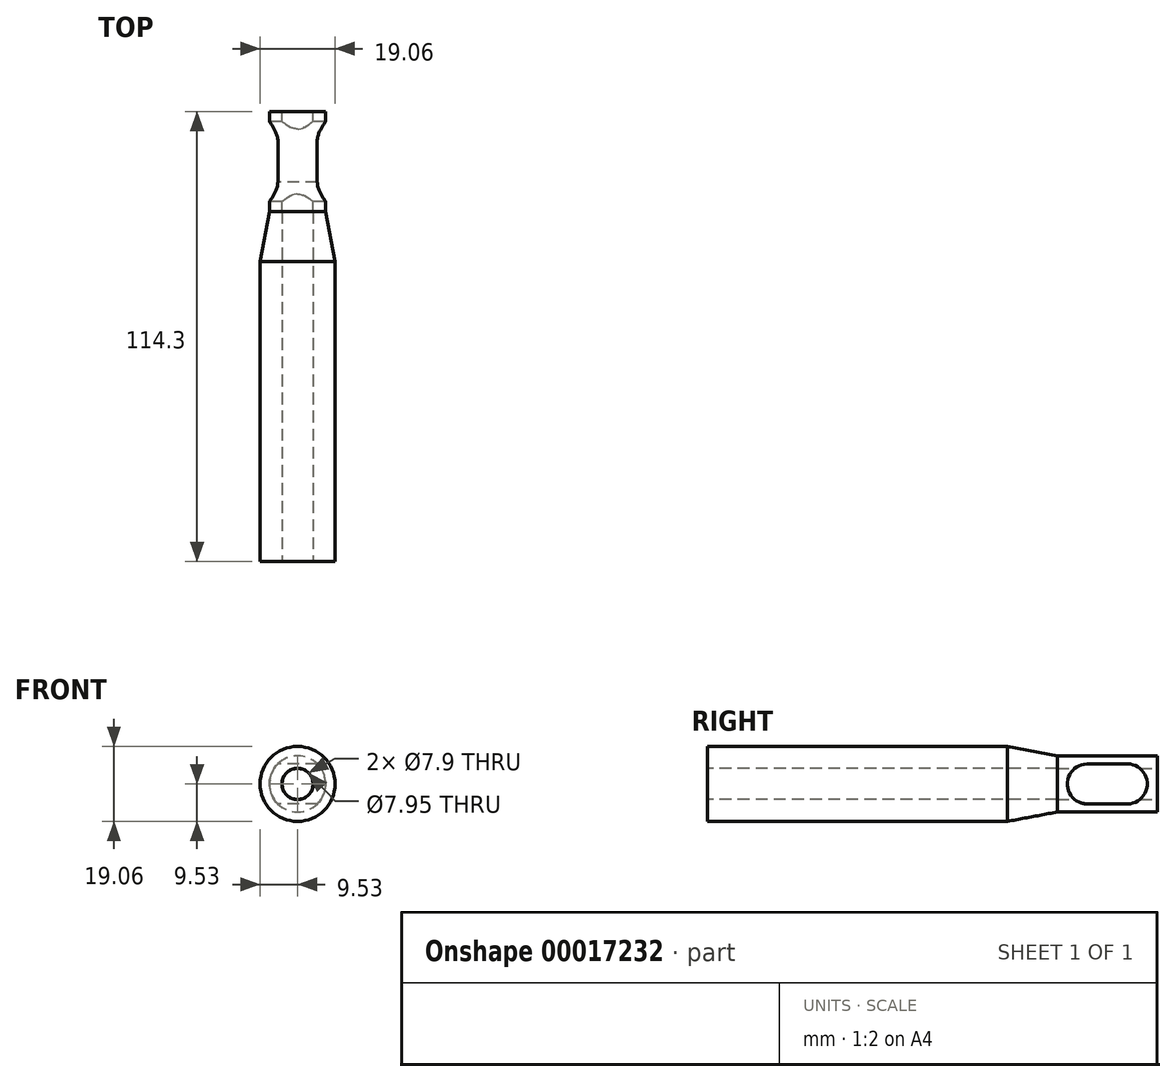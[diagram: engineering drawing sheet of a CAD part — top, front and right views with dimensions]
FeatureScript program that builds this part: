
annotation { "Feature Type Name" : "Feature", "Feature Type Description" : "" }
export const myFeature = defineFeature(function(context is Context, id is Id, definition is map)
    precondition{}
    {
        {
            var Q0;
            Q0=qCreatedBy(makeId("Front.planeOp"),FACE);
            var sketch = newSketch(context, id + "F0", { "sketchPlane" : qUnion([Q0])});
            skCircle(sketch, "E0.0", {"center": v(0, 0) * mm, "radius": 7.12 * mm});
            skSolve(sketch);
        }
        {
            var Q0;
            Q0=qCreatedBy(makeId("Top.planeOp"),FACE);
            var sketch = newSketch(context, id + "F1", { "sketchPlane" : qUnion([Q0])});
            skLineSegment(sketch, "E1", {"start": v(0, 0) * mm, "end": v(0, -25.4) * mm});
            skSolve(sketch);
        }
        {
            var Q0;
            Q0=makeQuery(id+"F0.imprint","IMPRINT",FACE,{"disambiguationData":[TD([[makeQuery(id+"F0.imprint","IMPRINT",EDGE,{"derivedFrom":sQuery(id+"F0.wireOp",EDGE,"093aef5c-26ce-4296-9acc-bf2fb9c0db15")}),-1.0]])]});
            var Q1;
            Q1=makeQuery(id+"F0.imprint","IMPRINT",FACE,{"disambiguationData":[TD([[makeQuery(id+"F0.imprint","IMPRINT",EDGE,{"derivedFrom":sQuery(id+"F0.wireOp",EDGE,"E0.0")}),1.0]])]});
            var Q2;
            Q2=sQuery(id+"F1.wireOp",EDGE,"E1");
            sweep(context, id + "F2", {"profiles" : qUnion([Q0, Q1]), "path" : qUnion([Q2])});
        }
        {
            var Q0;
            Q0=makeQuery(id+"F2.opSweep","CAP_FACE",FACE,{"disambiguationData":[OSD([sQuery(id+"F0.wireOp",EDGE,"093aef5c-26ce-4296-9acc-bf2fb9c0db15"),sQuery(id+"F0.wireOp",EDGE,"E0.0"),sQuery(id+"F1.wireOp",VERTEX,"E1.end")])],"isStart":false});
            var sketch = newSketch(context, id + "F3", { "sketchPlane" : qUnion([Q0])});
            skSolve(sketch);
        }
        {
            var Q0;
            Q0=qCreatedBy(makeId("Front.planeOp"),FACE);
            cPlane(context, id + "F4", {"entities" : qUnion([Q0]), "cplaneType" : CPlaneType.OFFSET, "offset" : 38.1 * mm, "width" : 152.4 * mm, "height" : 152.4 * mm});
        }
        {
            var Q0;
            Q0=qCreatedBy(id+"F4.planeOp",FACE);
            var sketch = newSketch(context, id + "F5", { "sketchPlane" : qUnion([Q0])});
            skCircle(sketch, "E2", {"center": v(0, 0) * mm, "radius": 9.53 * mm});
            skSolve(sketch);
        }
        {
            var Q0;
            Q0=makeQuery(id+"F3.imprint","IMPRINT",FACE,{"disambiguationData":[TD([[makeQuery(id+"F3.imprint","IMPRINT",EDGE,{"derivedFrom":makeQuery(id+"F2.opSweep","CAP_EDGE",EDGE,{"disambiguationData":[OSD([sQuery(id+"F0.wireOp",EDGE,"E0.0"),sQuery(id+"F1.wireOp",VERTEX,"E1.end")])],"isStart":false})}),1.0]])]});
            var Q1;
            Q1=makeQuery(id+"F5.imprint","IMPRINT",FACE,{"disambiguationData":[TD([[makeQuery(id+"F5.imprint","IMPRINT",EDGE,{"derivedFrom":sQuery(id+"F5.wireOp",EDGE,"E2")}),1.0]])]});
            loft(context, id + "F6", {"sheetProfilesArray" : [{ "sheetProfileEntities" : qUnion([Q0]) }, { "sheetProfileEntities" : qUnion([Q1]) }]});
        }
        {
            var Q0;
            Q0=qCreatedBy(makeId("Top.planeOp"),FACE);
            var sketch = newSketch(context, id + "F7", { "sketchPlane" : qUnion([Q0])});
            skLineSegment(sketch, "E3", {"start": v(0, -38.1) * mm, "end": v(0, -114.3) * mm});
            skSolve(sketch);
        }
        {
            var Q0;
            Q0=makeQuery(id+"F6.opLoft","CAP_FACE",FACE,{"disambiguationData":[OSD([makeQuery(id+"F5.imprint","IMPRINT",FACE,{"disambiguationData":[TD([[makeQuery(id+"F5.imprint","IMPRINT",EDGE,{"derivedFrom":sQuery(id+"F5.wireOp",EDGE,"E2")}),1.0]])]})])],"isStart":true});
            var Q1;
            Q1=sQuery(id+"F7.wireOp",EDGE,"E3");
            sweep(context, id + "F8", {"operationType" : NewBodyOperationType.ADD, "profiles" : qUnion([Q0]), "path" : qUnion([Q1])});
        }
        {
            var Q0;
            Q0=makeQuery(id+"F8.opSweep","CAP_FACE",FACE,{"disambiguationData":[OSD([makeQuery(id+"F5.imprint","IMPRINT",FACE,{"disambiguationData":[TD([[makeQuery(id+"F5.imprint","IMPRINT",EDGE,{"derivedFrom":sQuery(id+"F5.wireOp",EDGE,"E2")}),1.0]])]}),sQuery(id+"F7.wireOp",VERTEX,"E3.end")])],"isStart":false});
            var sketch = newSketch(context, id + "F9", { "sketchPlane" : qUnion([Q0])});
            skCircle(sketch, "E4", {"center": v(0, 0) * mm, "radius": 3.95 * mm});
            skSolve(sketch);
        }
        {
            var Q0;
            Q0=sQuery(id+"F9.wireOp",VERTEX,"E4.center");
            var Q1;
            Q1=makeQuery(id+"F6.opLoft","SWEPT_BODY",BODY,{"disambiguationData":[OSD([makeQuery(id+"F3.imprint","IMPRINT",FACE,{"disambiguationData":[TD([[makeQuery(id+"F3.imprint","IMPRINT",EDGE,{"derivedFrom":makeQuery(id+"F2.opSweep","CAP_EDGE",EDGE,{"disambiguationData":[OSD([sQuery(id+"F0.wireOp",EDGE,"E0.0"),sQuery(id+"F1.wireOp",VERTEX,"E1.end")])],"isStart":false})}),1.0]])]}),makeQuery(id+"F5.imprint","IMPRINT",FACE,{"disambiguationData":[TD([[makeQuery(id+"F5.imprint","IMPRINT",EDGE,{"derivedFrom":sQuery(id+"F5.wireOp",EDGE,"E2")}),1.0]])]})])]});
            hole(context, id + "F10", {"style" : HoleStyle.SIMPLE, "holeDiameter" : 7.95 * mm, "endStyle" : HoleEndStyle.THROUGH, "locations" : qUnion([Q0]), "scope" : qUnion([Q1])});
        }
        {
            var Q0;
            Q0=makeQuery(id+"F2.opSweep","CAP_FACE",FACE,{"disambiguationData":[OSD([sQuery(id+"F0.wireOp",EDGE,"E0.0"),sQuery(id+"F1.wireOp",VERTEX,"E1.start")])],"isStart":true});
            var sketch = newSketch(context, id + "F11", { "sketchPlane" : qUnion([Q0])});
            skCircle(sketch, "E5", {"center": v(0, 0) * mm, "radius": 3.95 * mm});
            skSolve(sketch);
        }
        {
            var Q0;
            Q0=sQuery(id+"F11.wireOp",VERTEX,"E5.center");
            var Q1;
            Q1=makeQuery(id+"F2.opSweep","SWEPT_BODY",BODY,{"disambiguationData":[OSD([sQuery(id+"F0.wireOp",EDGE,"E0.0"),sQuery(id+"F1.wireOp",EDGE,"E1")])]});
            hole(context, id + "F12", {"style" : HoleStyle.SIMPLE, "holeDiameter" : 7.9 * mm, "endStyle" : HoleEndStyle.THROUGH, "locations" : qUnion([Q0]), "scope" : qUnion([Q1])});
        }
        {
            var Q0;
            Q0=qCreatedBy(makeId("Right.planeOp"),FACE);
            var sketch = newSketch(context, id + "F13", { "sketchPlane" : qUnion([Q0])});
            skArc(sketch, "E6", {"start": v(-7.62, -5.08) * mm, "mid": v(-2.54, 0) * mm, "end": v(-7.62, 5.08) * mm});
            skArc(sketch, "E7", {"start": v(-17.69, 5.08) * mm, "mid": v(-22.86, -0.04) * mm, "end": v(-17.6, -5.08) * mm});
            skLineSegment(sketch, "E8", {"start": v(-17.87, 5.08) * mm, "end": v(-7.62, 5.08) * mm});
            skLineSegment(sketch, "E9", {"start": v(-17.96, -5.08) * mm, "end": v(-7.62, -5.08) * mm});
            skSolve(sketch);
        }
        {
            var Q0;
            {var subQ3=sQuery(id+"F13.wireOp",EDGE,"E6");Q0=makeQuery(id+"F13.imprint","IMPRINT",FACE,{"disambiguationData":[TD([[makeQuery(id+"F13.imprint","IMPRINT",EDGE,{"derivedFrom":subQ3}),1.0]])]});}
            extrude(context, id + "F14", {"entities" : qUnion([Q0]), "operationType" : NewBodyOperationType.REMOVE, "endBound" : BoundingType.THROUGH_ALL, "depth" : 25.4 * mm, "hasSecondDirection" : true, "secondDirectionOppositeDirection" : true, "secondDirectionDepth" : 25.4 * mm});
        }
    });
